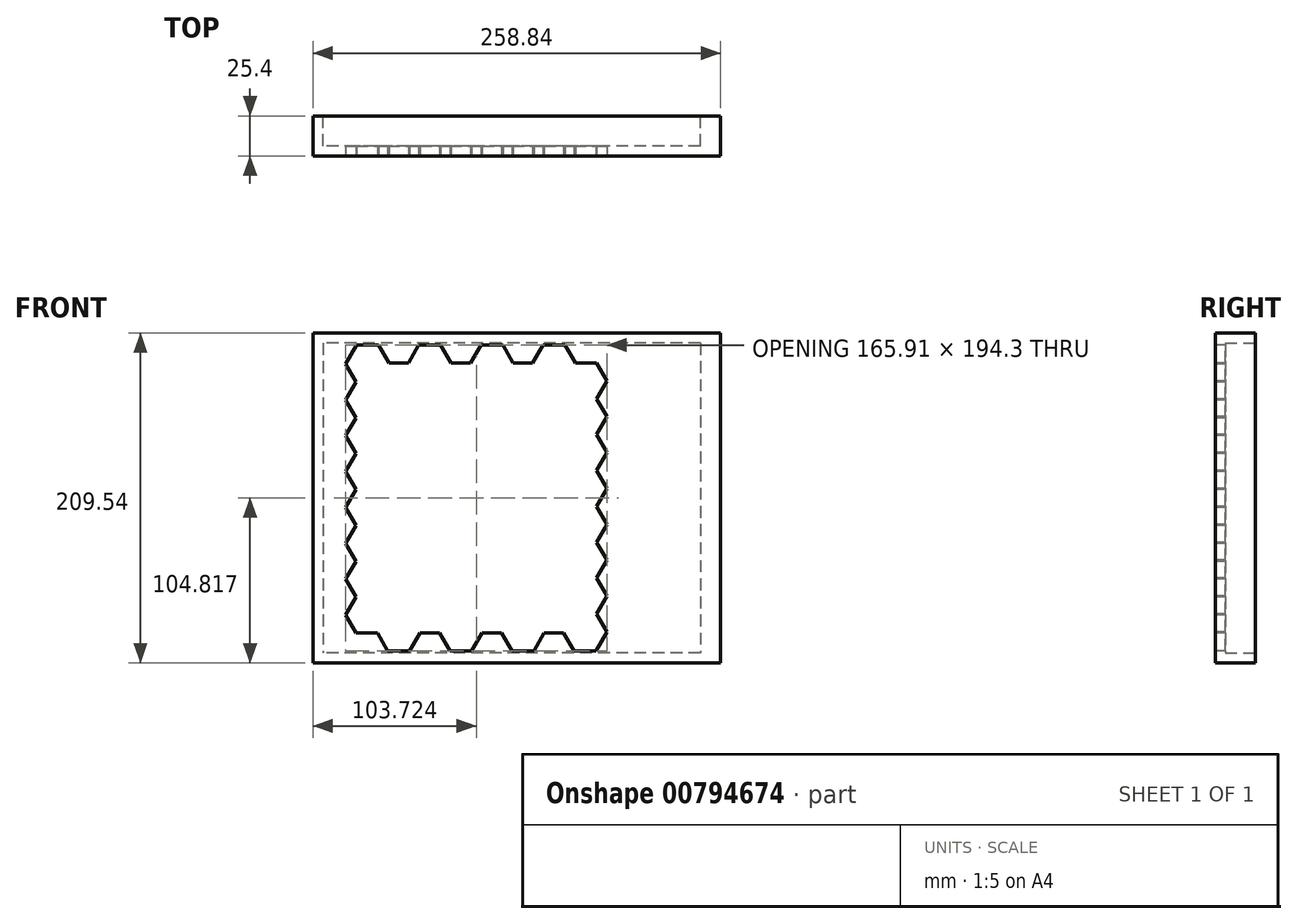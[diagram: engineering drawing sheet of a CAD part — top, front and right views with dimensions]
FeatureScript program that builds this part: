
annotation { "Feature Type Name" : "Feature", "Feature Type Description" : "" }
export const myFeature = defineFeature(function(context is Context, id is Id, definition is map)
    precondition{}
    {
        {
            var Q0;
            Q0=qCreatedBy(makeId("Front.planeOp"),FACE);
            var sketch = newSketch(context, id + "F0", { "sketchPlane" : qUnion([Q0])});
            skLineSegment(sketch, "E0", {"start": v(-82.07, 74.66) * mm, "end": v(-88.65, 63.27) * mm});
            skLineSegment(sketch, "E1", {"start": v(-88.65, 63.27) * mm, "end": v(-82.07, 51.88) * mm});
            skLineSegment(sketch, "E2", {"start": v(-82.07, 51.88) * mm, "end": v(-88.65, 40.49) * mm});
            skLineSegment(sketch, "E3", {"start": v(-88.65, 40.49) * mm, "end": v(-82.07, 29.1) * mm});
            skLineSegment(sketch, "E4", {"start": v(-82.07, 29.1) * mm, "end": v(-88.65, 17.7) * mm});
            skLineSegment(sketch, "E5", {"start": v(-88.65, 17.7) * mm, "end": v(-82.07, 6.31) * mm});
            skLineSegment(sketch, "E6", {"start": v(-82.07, 6.31) * mm, "end": v(-88.65, -5.08) * mm});
            skLineSegment(sketch, "E7", {"start": v(-88.65, -5.08) * mm, "end": v(-82.07, -16.47) * mm});
            skLineSegment(sketch, "E8", {"start": v(-82.07, -16.47) * mm, "end": v(-88.65, -27.86) * mm});
            skLineSegment(sketch, "E9", {"start": v(-88.65, -27.86) * mm, "end": v(-82.07, -39.26) * mm});
            skLineSegment(sketch, "E10", {"start": v(-82.07, -39.26) * mm, "end": v(-88.65, -50.65) * mm});
            skLineSegment(sketch, "E11", {"start": v(-88.65, -50.65) * mm, "end": v(-82.07, -62.04) * mm});
            skLineSegment(sketch, "E12", {"start": v(-82.07, -62.04) * mm, "end": v(-88.65, -73.43) * mm});
            skLineSegment(sketch, "E13", {"start": v(-88.65, -73.43) * mm, "end": v(-82.07, -84.82) * mm});
            skLineSegment(sketch, "E14", {"start": v(-82.07, -84.82) * mm, "end": v(-68.55, -84.81) * mm});
            skLineSegment(sketch, "E15", {"start": v(-68.55, -84.81) * mm, "end": v(-61.98, -96.2) * mm});
            skLineSegment(sketch, "E16", {"start": v(-61.98, -96.2) * mm, "end": v(-48.07, -96.2) * mm});
            skLineSegment(sketch, "E17", {"start": v(-48.07, -96.2) * mm, "end": v(-41.5, -84.81) * mm});
            skLineSegment(sketch, "E18", {"start": v(-41.5, -84.81) * mm, "end": v(-29.1, -84.81) * mm});
            skLineSegment(sketch, "E19", {"start": v(-29.1, -84.81) * mm, "end": v(-22.51, -96.2) * mm});
            skLineSegment(sketch, "E20", {"start": v(-22.51, -96.2) * mm, "end": v(-8.61, -96.2) * mm});
            skLineSegment(sketch, "E21", {"start": v(-8.61, -96.2) * mm, "end": v(-2.03, -84.81) * mm});
            skLineSegment(sketch, "E22", {"start": v(-2.03, -84.81) * mm, "end": v(10.37, -84.81) * mm});
            skLineSegment(sketch, "E23", {"start": v(10.37, -84.81) * mm, "end": v(16.95, -96.2) * mm});
            skLineSegment(sketch, "E24", {"start": v(16.95, -96.2) * mm, "end": v(30.85, -96.2) * mm});
            skLineSegment(sketch, "E25", {"start": v(30.85, -96.2) * mm, "end": v(37.43, -84.81) * mm});
            skLineSegment(sketch, "E26", {"start": v(37.43, -84.81) * mm, "end": v(49.84, -84.81) * mm});
            skLineSegment(sketch, "E27", {"start": v(49.84, -84.81) * mm, "end": v(56.41, -96.2) * mm});
            skLineSegment(sketch, "E28", {"start": v(56.41, -96.2) * mm, "end": v(70.3, -96.2) * mm});
            skLineSegment(sketch, "E29", {"start": v(70.3, -96.2) * mm, "end": v(77.26, -84.16) * mm});
            skLineSegment(sketch, "E30", {"start": v(77.26, -84.16) * mm, "end": v(70.68, -72.77) * mm});
            skLineSegment(sketch, "E31", {"start": v(70.68, -72.77) * mm, "end": v(77.26, -61.38) * mm});
            skLineSegment(sketch, "E32", {"start": v(77.26, -61.38) * mm, "end": v(70.68, -49.99) * mm});
            skLineSegment(sketch, "E33", {"start": v(70.68, -49.99) * mm, "end": v(77.26, -38.6) * mm});
            skLineSegment(sketch, "E34", {"start": v(77.26, -38.6) * mm, "end": v(70.68, -27.2) * mm});
            skLineSegment(sketch, "E35", {"start": v(70.68, -27.2) * mm, "end": v(77.26, -15.81) * mm});
            skLineSegment(sketch, "E36", {"start": v(77.26, -15.81) * mm, "end": v(70.68, -4.42) * mm});
            skLineSegment(sketch, "E37", {"start": v(70.68, -4.42) * mm, "end": v(77.26, 6.97) * mm});
            skLineSegment(sketch, "E38", {"start": v(77.26, 6.97) * mm, "end": v(70.68, 18.36) * mm});
            skLineSegment(sketch, "E39", {"start": v(70.68, 18.36) * mm, "end": v(77.26, 29.76) * mm});
            skLineSegment(sketch, "E40", {"start": v(77.26, 29.76) * mm, "end": v(70.68, 41.15) * mm});
            skLineSegment(sketch, "E41", {"start": v(70.68, 41.15) * mm, "end": v(77.26, 52.54) * mm});
            skLineSegment(sketch, "E42", {"start": v(77.26, 52.54) * mm, "end": v(70.68, 63.93) * mm});
            skLineSegment(sketch, "E43", {"start": v(70.68, 63.93) * mm, "end": v(77.26, 75.32) * mm});
            skLineSegment(sketch, "E44", {"start": v(77.26, 75.32) * mm, "end": v(70.68, 86.72) * mm});
            skLineSegment(sketch, "E45", {"start": v(70.68, 86.72) * mm, "end": v(57.16, 86.7) * mm});
            skLineSegment(sketch, "E46", {"start": v(57.16, 86.7) * mm, "end": v(50.59, 98.1) * mm});
            skLineSegment(sketch, "E47", {"start": v(50.59, 98.1) * mm, "end": v(36.68, 98.1) * mm});
            skLineSegment(sketch, "E48", {"start": v(36.68, 98.1) * mm, "end": v(30.1, 86.7) * mm});
            skLineSegment(sketch, "E49", {"start": v(30.1, 86.7) * mm, "end": v(17.7, 86.7) * mm});
            skLineSegment(sketch, "E50", {"start": v(17.7, 86.7) * mm, "end": v(11.12, 98.1) * mm});
            skLineSegment(sketch, "E51", {"start": v(11.12, 98.1) * mm, "end": v(-2.78, 98.1) * mm});
            skLineSegment(sketch, "E52", {"start": v(-2.78, 98.1) * mm, "end": v(-9.36, 86.7) * mm});
            skLineSegment(sketch, "E53", {"start": v(-9.36, 86.7) * mm, "end": v(-21.77, 86.7) * mm});
            skLineSegment(sketch, "E54", {"start": v(-21.77, 86.7) * mm, "end": v(-28.34, 98.1) * mm});
            skLineSegment(sketch, "E55", {"start": v(-28.34, 98.1) * mm, "end": v(-42.25, 98.1) * mm});
            skLineSegment(sketch, "E56", {"start": v(-42.25, 98.1) * mm, "end": v(-48.83, 86.7) * mm});
            skLineSegment(sketch, "E57", {"start": v(-48.83, 86.7) * mm, "end": v(-61.24, 86.7) * mm});
            skLineSegment(sketch, "E58", {"start": v(-61.24, 86.7) * mm, "end": v(-67.81, 98.1) * mm});
            skLineSegment(sketch, "E59", {"start": v(-67.81, 98.1) * mm, "end": v(-81.7, 98.1) * mm});
            skLineSegment(sketch, "E60", {"start": v(-81.7, 98.1) * mm, "end": v(-88.65, 86.06) * mm});
            skLineSegment(sketch, "E61", {"start": v(-88.65, 86.06) * mm, "end": v(-82.07, 74.66) * mm});
            skSolve(sketch);
        }
        {
            var Q0;
            Q0=qCreatedBy(makeId("Front.planeOp"),FACE);
            var sketch = newSketch(context, id + "F1", { "sketchPlane" : qUnion([Q0])});
            skLineSegment(sketch, "E62.bottom", {"start": v(-109.42, 105.67) * mm, "end": v(149.42, 105.67) * mm});
            skLineSegment(sketch, "E62.top", {"start": v(-109.42, -103.87) * mm, "end": v(149.42, -103.87) * mm});
            skLineSegment(sketch, "E62.left", {"start": v(-109.42, 105.67) * mm, "end": v(-109.42, -103.87) * mm});
            skLineSegment(sketch, "E62.right", {"start": v(149.42, 105.67) * mm, "end": v(149.42, -103.87) * mm});
            skSolve(sketch);
        }
        {
            var Q0;
            Q0 = qSketchRegion(id + "F1", true);
            extrude(context, id + "F2", {"entities" : qUnion([Q0]), "oppositeDirection" : true, "depth" : 25.4 * mm, "offsetDistance" : 25.4 * mm});
        }
        {
            var Q0;
            Q0 = qSketchRegion(id + "F0", true);
            extrude(context, id + "F3", {"entities" : qUnion([Q0]), "operationType" : NewBodyOperationType.REMOVE, "oppositeDirection" : true, "depth" : 25.4 * mm, "offsetDistance" : 25.4 * mm});
        }
        {
            var Q0;
            Q0=makeQuery(id+"F2.opExtrude","CAP_FACE",FACE,{"disambiguationData":[OSD([sQuery(id+"F1.wireOp",EDGE,"E62.bottom"),sQuery(id+"F1.wireOp",EDGE,"E62.top"),sQuery(id+"F1.wireOp",EDGE,"E62.left"),sQuery(id+"F1.wireOp",EDGE,"E62.right")])],"isStart":false});
            var sketch = newSketch(context, id + "F4", { "sketchPlane" : qUnion([Q0])});
            skLineSegment(sketch, "E63.bottom", {"start": v(-136.72, 99.32) * mm, "end": v(103.07, 99.32) * mm});
            skLineSegment(sketch, "E63.top", {"start": v(-136.72, -97.52) * mm, "end": v(103.07, -97.52) * mm});
            skLineSegment(sketch, "E63.left", {"start": v(-136.72, 99.32) * mm, "end": v(-136.72, -97.52) * mm});
            skLineSegment(sketch, "E63.right", {"start": v(103.07, 99.32) * mm, "end": v(103.07, -97.52) * mm});
            skSolve(sketch);
        }
        {
            var Q0;
            Q0 = qSketchRegion(id + "F4", true);
            extrude(context, id + "F5", {"entities" : qUnion([Q0]), "operationType" : NewBodyOperationType.REMOVE, "oppositeDirection" : true, "depth" : 19.05 * mm, "offsetDistance" : 25.4 * mm});
        }
    });
